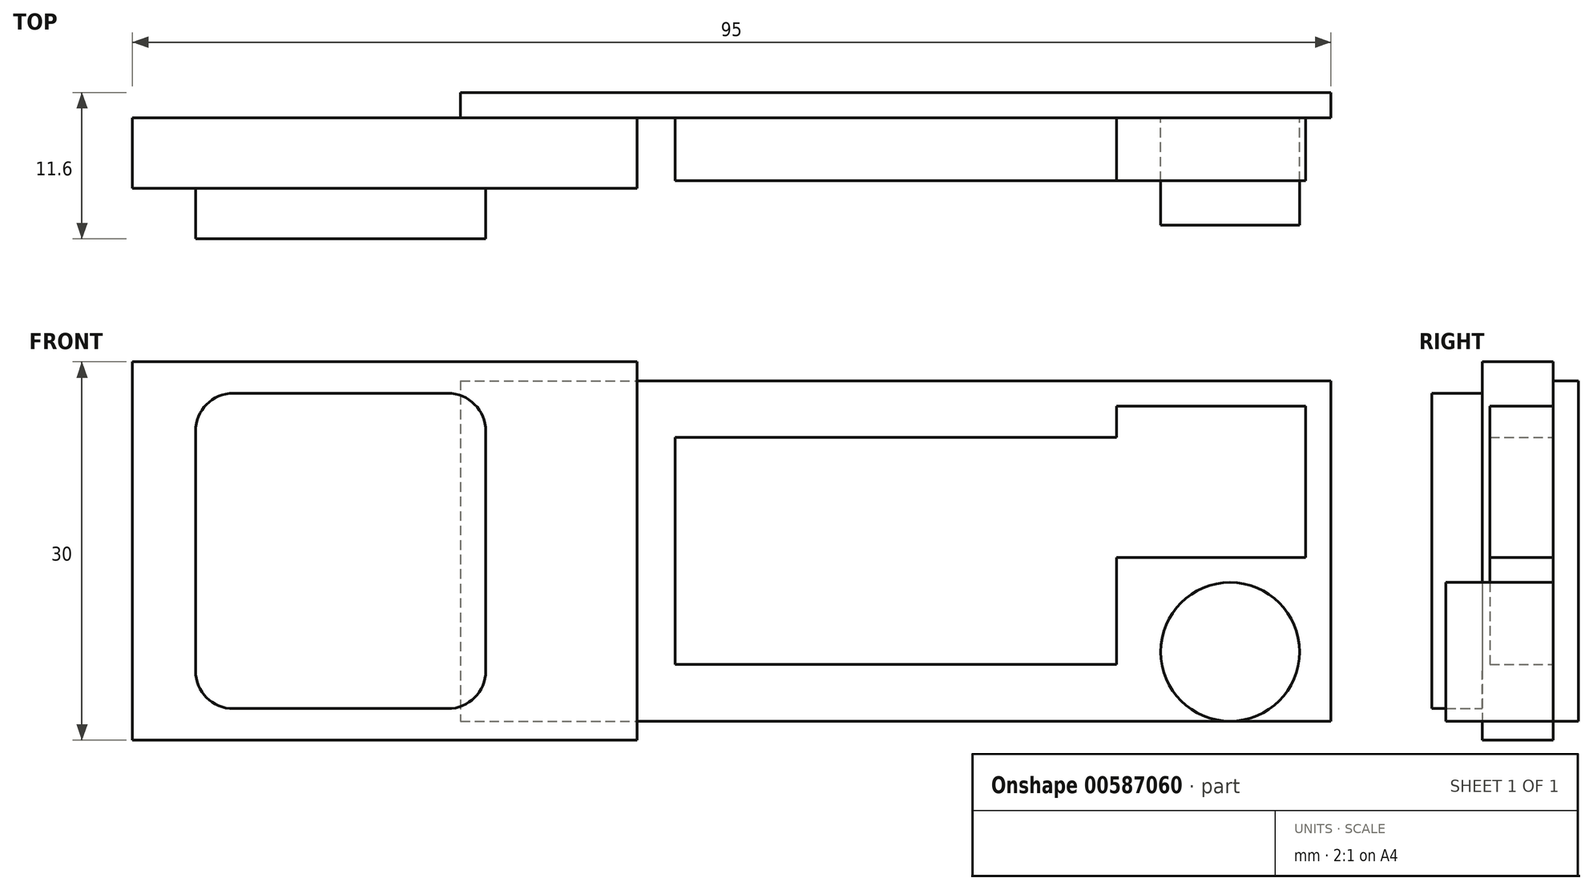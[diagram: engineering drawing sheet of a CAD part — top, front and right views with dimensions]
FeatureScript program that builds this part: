
annotation { "Feature Type Name" : "Feature", "Feature Type Description" : "" }
export const myFeature = defineFeature(function(context is Context, id is Id, definition is map)
    precondition{}
    {
        {
            var Q0;
            Q0=qCreatedBy(makeId("Front.planeOp"),FACE);
            var sketch = newSketch(context, id + "F0", { "sketchPlane" : qUnion([Q0])});
            skLineSegment(sketch, "E0.bottom", {"start": v(-34.5, 13.5) * mm, "end": v(34.5, 13.5) * mm});
            skLineSegment(sketch, "E0.top", {"start": v(-34.5, -13.5) * mm, "end": v(34.5, -13.5) * mm});
            skLineSegment(sketch, "E0.left", {"start": v(-34.5, 13.5) * mm, "end": v(-34.5, -13.5) * mm});
            skLineSegment(sketch, "E0.right", {"start": v(34.5, 13.5) * mm, "end": v(34.5, -13.5) * mm});
            skLineSegment(sketch, "E1", {"start": v(34.5, 13.5) * mm, "end": v(-34.5, -13.5) * mm, "construction": true});
            skLineSegment(sketch, "E2", {"start": v(-34.5, 13.5) * mm, "end": v(34.5, -13.5) * mm, "construction": true});
            skSolve(sketch);
        }
        {
            var Q0;
            Q0=qSketchRegion(id+"F0",true);
            extrude(context, id + "F1", {"entities" : qUnion([Q0]), "depth" : 2 * mm});
        }
        {
            var Q0;
            Q0=makeQuery(id+"F1.opExtrude","CAP_FACE",FACE,{"disambiguationData":[OSD([sQuery(id+"F0.wireOp",EDGE,"E0.bottom"),sQuery(id+"F0.wireOp",EDGE,"E0.top"),sQuery(id+"F0.wireOp",EDGE,"E0.left"),sQuery(id+"F0.wireOp",EDGE,"E0.right")])],"isStart":false});
            var sketch = newSketch(context, id + "F2", { "sketchPlane" : qUnion([Q0])});
            skLineSegment(sketch, "E3.bottom", {"start": v(-60.5, 15) * mm, "end": v(-20.5, 15) * mm});
            skLineSegment(sketch, "E3.top", {"start": v(-60.5, -15) * mm, "end": v(-20.5, -15) * mm});
            skLineSegment(sketch, "E3.left", {"start": v(-60.5, 15) * mm, "end": v(-60.5, -15) * mm});
            skLineSegment(sketch, "E3.right", {"start": v(-20.5, 15) * mm, "end": v(-20.5, -15) * mm});
            skSolve(sketch);
        }
        {
            var Q0;
            Q0=qSketchRegion(id+"F2",true);
            extrude(context, id + "F3", {"entities" : qUnion([Q0]), "operationType" : NewBodyOperationType.ADD, "depth" : 5.6 * mm});
        }
        {
            var Q0;
            Q0=makeQuery(id+"F1.opExtrude","CAP_FACE",FACE,{"disambiguationData":[OSD([sQuery(id+"F0.wireOp",EDGE,"E0.bottom"),sQuery(id+"F0.wireOp",EDGE,"E0.top"),sQuery(id+"F0.wireOp",EDGE,"E0.left"),sQuery(id+"F0.wireOp",EDGE,"E0.right")])],"isStart":false});
            var sketch = newSketch(context, id + "F4", { "sketchPlane" : qUnion([Q0])});
            skLineSegment(sketch, "E4.bottom", {"start": v(-17.5, 9) * mm, "end": v(17.5, 9) * mm});
            skLineSegment(sketch, "E4.top", {"start": v(-17.5, -9) * mm, "end": v(17.5, -9) * mm});
            skLineSegment(sketch, "E4.left", {"start": v(-17.5, 9) * mm, "end": v(-17.5, -9) * mm});
            skLineSegment(sketch, "E4.right", {"start": v(17.5, 9) * mm, "end": v(17.5, -9) * mm});
            skSolve(sketch);
        }
        {
            var Q0;
            Q0=qSketchRegion(id+"F4",true);
            extrude(context, id + "F5", {"entities" : qUnion([Q0]), "operationType" : NewBodyOperationType.ADD, "depth" : 5 * mm});
        }
        {
            var Q0;
            Q0=makeQuery(id+"F1.opExtrude","CAP_FACE",FACE,{"disambiguationData":[OSD([sQuery(id+"F0.wireOp",EDGE,"E0.bottom"),sQuery(id+"F0.wireOp",EDGE,"E0.top"),sQuery(id+"F0.wireOp",EDGE,"E0.left"),sQuery(id+"F0.wireOp",EDGE,"E0.right")])],"isStart":false});
            var sketch = newSketch(context, id + "F6", { "sketchPlane" : qUnion([Q0])});
            skLineSegment(sketch, "E5.bottom", {"start": v(17.5, 11.5) * mm, "end": v(32.5, 11.5) * mm});
            skLineSegment(sketch, "E5.top", {"start": v(17.5, -0.5) * mm, "end": v(32.5, -0.5) * mm});
            skLineSegment(sketch, "E5.left", {"start": v(17.5, 11.5) * mm, "end": v(17.5, -0.5) * mm});
            skLineSegment(sketch, "E5.right", {"start": v(32.5, 11.5) * mm, "end": v(32.5, -0.5) * mm});
            skSolve(sketch);
        }
        {
            var Q0;
            Q0=qSketchRegion(id+"F6",true);
            extrude(context, id + "F7", {"entities" : qUnion([Q0]), "operationType" : NewBodyOperationType.ADD, "depth" : 5 * mm});
        }
        {
            var Q0;
            Q0=makeQuery(id+"F1.opExtrude","CAP_FACE",FACE,{"disambiguationData":[OSD([sQuery(id+"F0.wireOp",EDGE,"E0.bottom"),sQuery(id+"F0.wireOp",EDGE,"E0.top"),sQuery(id+"F0.wireOp",EDGE,"E0.left"),sQuery(id+"F0.wireOp",EDGE,"E0.right")])],"isStart":false});
            var sketch = newSketch(context, id + "F8", { "sketchPlane" : qUnion([Q0])});
            skCircle(sketch, "E6", {"center": v(26.5, -8) * mm, "radius": 5.5 * mm});
            skSolve(sketch);
        }
        {
            var Q0;
            Q0=qSketchRegion(id+"F8",true);
            extrude(context, id + "F9", {"entities" : qUnion([Q0]), "operationType" : NewBodyOperationType.ADD, "depth" : 8.5 * mm});
        }
        {
            var Q0;
            Q0=makeQuery(id+"F3.opExtrude","CAP_FACE",FACE,{"disambiguationData":[OSD([sQuery(id+"F2.wireOp",EDGE,"E3.bottom"),sQuery(id+"F2.wireOp",EDGE,"E3.top"),sQuery(id+"F2.wireOp",EDGE,"E3.left"),sQuery(id+"F2.wireOp",EDGE,"E3.right")])],"isStart":false});
            var sketch = newSketch(context, id + "F10", { "sketchPlane" : qUnion([Q0])});
            skLineSegment(sketch, "E7.bottom", {"start": v(-52.5, 12.5) * mm, "end": v(-35.5, 12.5) * mm});
            skLineSegment(sketch, "E7.top", {"start": v(-52.5, -12.5) * mm, "end": v(-35.5, -12.5) * mm});
            skLineSegment(sketch, "E7.left", {"start": v(-55.5, 9.5) * mm, "end": v(-55.5, -9.5) * mm});
            skLineSegment(sketch, "E7.right", {"start": v(-32.5, 9.5) * mm, "end": v(-32.5, -9.5) * mm});
            skPoint(sketch, "E8.visualSharp", {"position": v(-55.5, 12.5) * mm});
            skArc(sketch, "E8.filletArc", {"start": v(-52.5, 12.5) * mm, "mid": v(-54.62, 11.62) * mm, "end": v(-55.5, 9.5) * mm});
            skPoint(sketch, "E9.visualSharp", {"position": v(-32.5, 12.5) * mm});
            skArc(sketch, "E9.filletArc", {"start": v(-32.5, 9.5) * mm, "mid": v(-33.38, 11.62) * mm, "end": v(-35.5, 12.5) * mm});
            skPoint(sketch, "E10.visualSharp", {"position": v(-32.5, -12.5) * mm});
            skArc(sketch, "E10.filletArc", {"start": v(-35.5, -12.5) * mm, "mid": v(-33.38, -11.62) * mm, "end": v(-32.5, -9.5) * mm});
            skPoint(sketch, "E11.visualSharp", {"position": v(-55.5, -12.5) * mm});
            skArc(sketch, "E11.filletArc", {"start": v(-55.5, -9.5) * mm, "mid": v(-54.62, -11.62) * mm, "end": v(-52.5, -12.5) * mm});
            skSolve(sketch);
        }
        {
            var Q0;
            Q0 = qSketchRegion(id + "F10", true);
            extrude(context, id + "F11", {"entities" : qUnion([Q0]), "operationType" : NewBodyOperationType.ADD, "depth" : 4 * mm});
        }
    });
